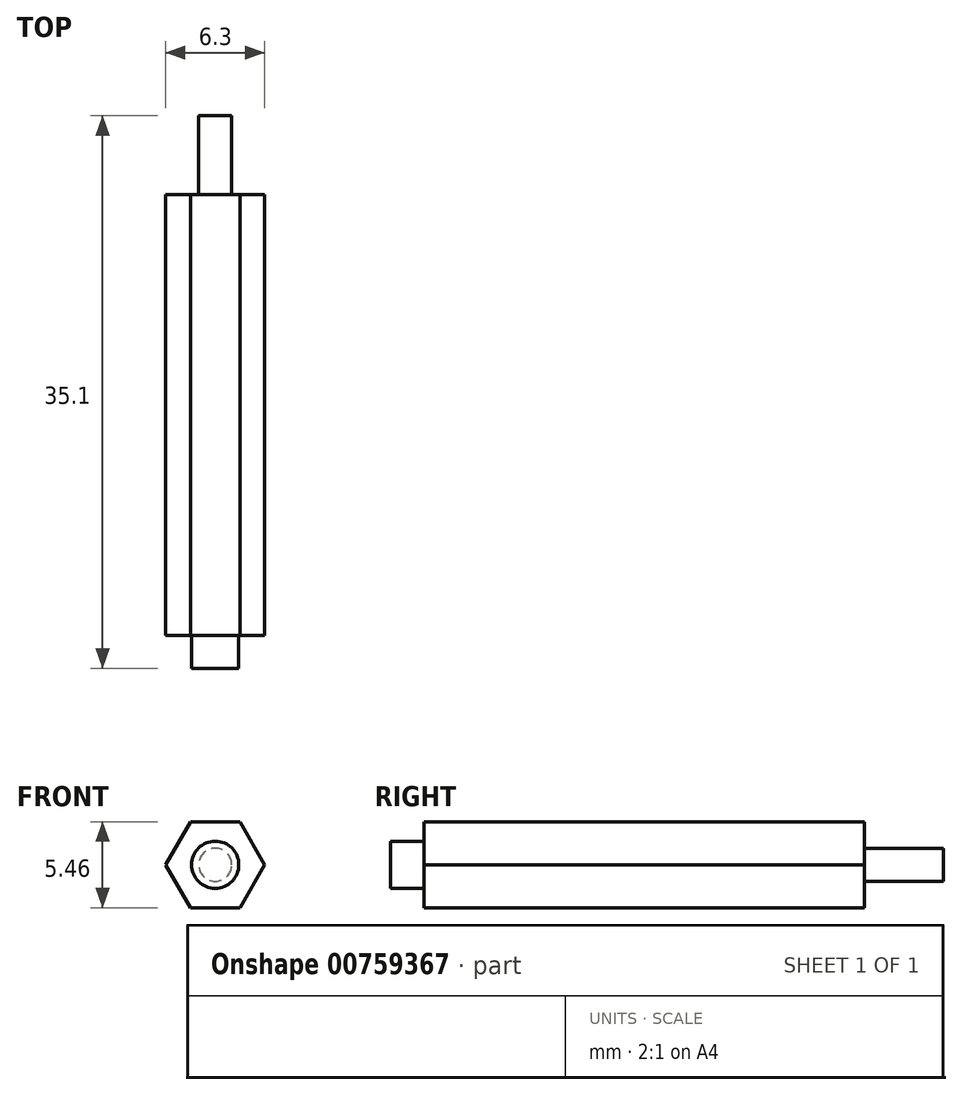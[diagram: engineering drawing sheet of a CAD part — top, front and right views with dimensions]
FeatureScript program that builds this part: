
annotation { "Feature Type Name" : "Feature", "Feature Type Description" : "" }
export const myFeature = defineFeature(function(context is Context, id is Id, definition is map)
    precondition{}
    {
        {
            var Q0;
            Q0=qCreatedBy(makeId("Front.planeOp"),FACE);
            var sketch = newSketch(context, id + "F0", { "sketchPlane" : qUnion([Q0])});
            skCircle(sketch, "E0.cCircle", {"center": v(0, 0) * mm, "radius": 2.73 * mm, "construction": true});
            skLineSegment(sketch, "E0.0", {"start": v(-1.57, 2.73) * mm, "end": v(1.57, 2.73) * mm});
            skLineSegment(sketch, "E0.1", {"start": v(1.58, 2.73) * mm, "end": v(3.15, 0) * mm});
            skLineSegment(sketch, "E0.2", {"start": v(3.15, 0) * mm, "end": v(1.57, -2.73) * mm});
            skLineSegment(sketch, "E0.3", {"start": v(1.58, -2.73) * mm, "end": v(-1.57, -2.73) * mm});
            skLineSegment(sketch, "E0.4", {"start": v(-1.57, -2.73) * mm, "end": v(-3.15, 0) * mm});
            skLineSegment(sketch, "E0.5", {"start": v(-3.15, 0) * mm, "end": v(-1.57, 2.73) * mm});
            skPoint(sketch, "E0.0.midPoint", {"position": v(0, 2.73) * mm});
            skSolve(sketch);
        }
        {
            var Q0;
            Q0 = qSketchRegion(id + "F0", true);
            extrude(context, id + "F1", {"entities" : qUnion([Q0]), "depth" : 28 * mm, "offsetDistance" : 25 * mm});
        }
        {
            var Q0;
            Q0=makeQuery(id+"F1.opExtrude","CAP_FACE",FACE,{"disambiguationData":[OSD([sQuery(id+"F0.wireOp",EDGE,"E0.0"),sQuery(id+"F0.wireOp",EDGE,"E0.1"),sQuery(id+"F0.wireOp",EDGE,"E0.2"),sQuery(id+"F0.wireOp",EDGE,"E0.3"),sQuery(id+"F0.wireOp",EDGE,"E0.4"),sQuery(id+"F0.wireOp",EDGE,"E0.5")])],"isStart":false});
            var sketch = newSketch(context, id + "F2", { "sketchPlane" : qUnion([Q0])});
            skCircle(sketch, "E1", {"center": v(0, 0) * mm, "radius": 1.5 * mm});
            skSolve(sketch);
        }
        {
            var Q0;
            Q0 = qSketchRegion(id + "F2", true);
            extrude(context, id + "F3", {"entities" : qUnion([Q0]), "operationType" : NewBodyOperationType.ADD, "depth" : 2.1 * mm, "offsetDistance" : 25 * mm});
        }
        {
            var Q0;
            Q0=makeQuery(id+"F1.opExtrude","CAP_FACE",FACE,{"disambiguationData":[OSD([sQuery(id+"F0.wireOp",EDGE,"E0.0"),sQuery(id+"F0.wireOp",EDGE,"E0.1"),sQuery(id+"F0.wireOp",EDGE,"E0.2"),sQuery(id+"F0.wireOp",EDGE,"E0.3"),sQuery(id+"F0.wireOp",EDGE,"E0.4"),sQuery(id+"F0.wireOp",EDGE,"E0.5")])],"isStart":true});
            var sketch = newSketch(context, id + "F4", { "sketchPlane" : qUnion([Q0])});
            skCircle(sketch, "E2", {"center": v(0, 0) * mm, "radius": 1.05 * mm});
            skSolve(sketch);
        }
        {
            var Q0;
            Q0=makeQuery(id+"F4.imprint","IMPRINT",FACE,{"disambiguationData":[TD([[makeQuery(id+"F4.imprint","IMPRINT",EDGE,{"derivedFrom":sQuery(id+"F4.wireOp",EDGE,"E2")}),1.0]])]});
            extrude(context, id + "F5", {"entities" : qUnion([Q0]), "operationType" : NewBodyOperationType.ADD, "depth" : 5 * mm, "offsetDistance" : 25 * mm});
        }
    });
